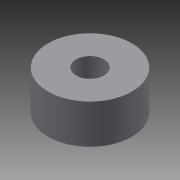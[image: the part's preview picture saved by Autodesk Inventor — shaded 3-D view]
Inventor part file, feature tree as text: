
AUTODESK INVENTOR PART (.ipt)
format: ipt  version: 2013 (Build 170138000, 138)  size: 72,192 bytes
history: native  units: in
note: dims shown in document units (in); Inventor stores cm internally (conversion verified against a paired STEP export)
features: extrude x1, sketch x1
ambient origin geometry x8: Origin, YZ Plane, XZ Plane, XY Plane, X Axis, Y Axis, Z Axis, Center Point
bodies: Solid1 (feature_tree)
feature tree (2):
  extrude  "Extrusion1"  Depth=1.1811in
  sketch  "Sketch1"  dims[d0=0.3937in d1=1.1811in d2=0.5512in d3=0.0in]
